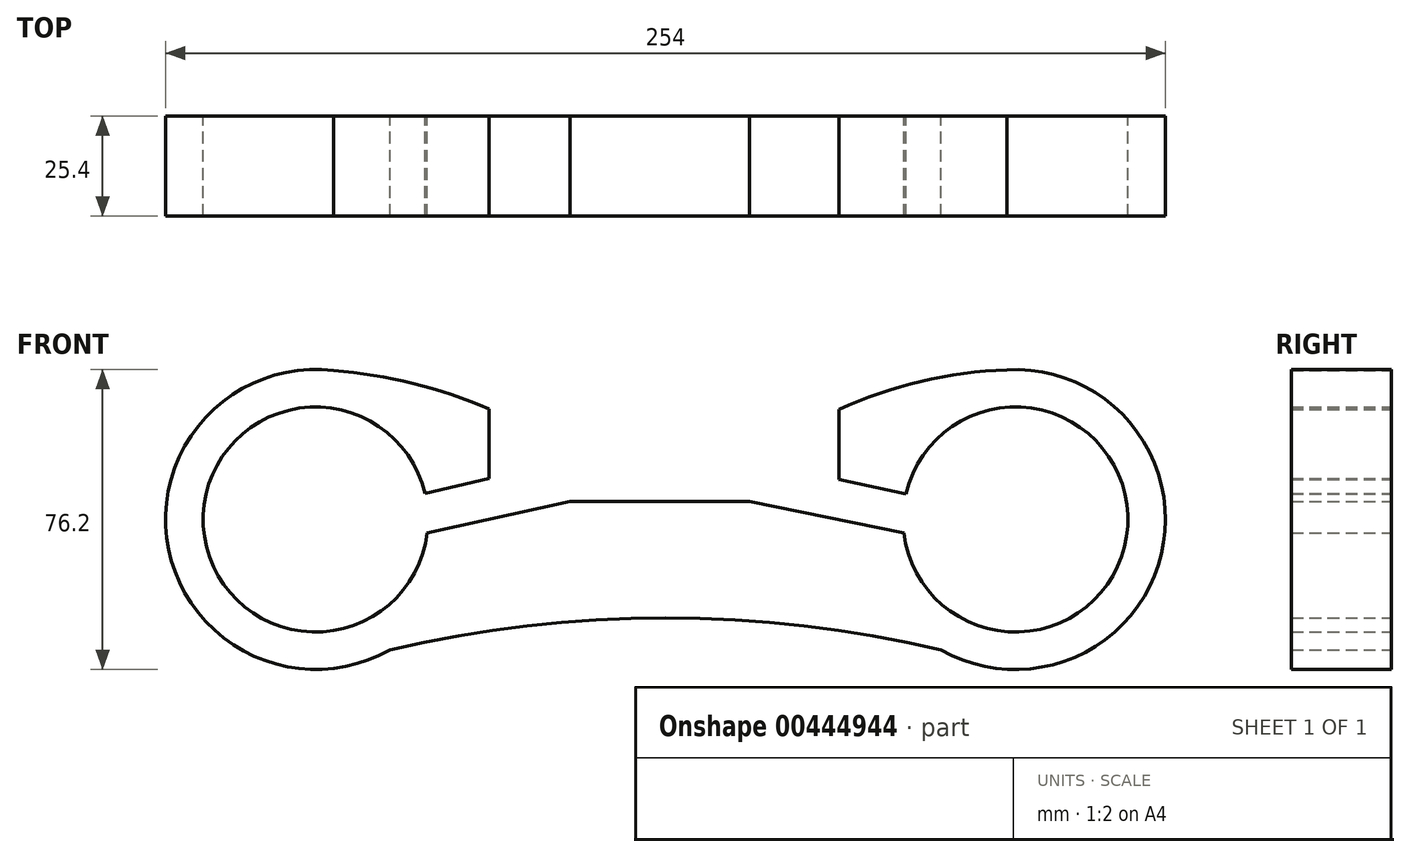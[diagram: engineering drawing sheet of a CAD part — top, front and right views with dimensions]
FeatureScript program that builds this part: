
annotation { "Feature Type Name" : "Feature", "Feature Type Description" : "" }
export const myFeature = defineFeature(function(context is Context, id is Id, definition is map)
    precondition{}
    {
        {
            var Q0;
            Q0=qCreatedBy(makeId("Front.planeOp"),FACE);
            var sketch = newSketch(context, id + "F0", { "sketchPlane" : qUnion([Q0])});
            skArc(sketch, "E0", {"start": v(-54.1, 9.54) * mm, "mid": v(-129.1, -2.98) * mm, "end": v(-53.1, -0.47) * mm});
            skArc(sketch, "E1", {"start": v(48.55, -0.64) * mm, "mid": v(124.55, -2.8) * mm, "end": v(49.5, 9.34) * mm});
            skArc(sketch, "E2", {"start": v(86.62, -37.3) * mm, "mid": v(-2.28, -24.27) * mm, "end": v(-91.18, -37.3) * mm});
            skArc(sketch, "E3", {"start": v(-63.38, 7.38) * mm, "mid": v(-119.7, -0.84) * mm, "end": v(-62.8, -2.6) * mm});
            skArc(sketch, "E4", {"start": v(58.25, -2.6) * mm, "mid": v(115.15, -0.8) * mm, "end": v(58.8, 7.33) * mm});
            skLineSegment(sketch, "E5", {"start": v(-26.59, 5.32) * mm, "end": v(19, 5.32) * mm});
            skLineSegment(sketch, "E6", {"start": v(-47.1, 11.17) * mm, "end": v(-63.38, 7.38) * mm});
            skLineSegment(sketch, "E7", {"start": v(-62.8, -2.6) * mm, "end": v(-26.59, 5.32) * mm});
            skLineSegment(sketch, "E8", {"start": v(41.8, 11) * mm, "end": v(58.8, 7.33) * mm});
            skLineSegment(sketch, "E9", {"start": v(58.25, -2.6) * mm, "end": v(19, 5.32) * mm});
            skLineSegment(sketch, "E10.top", {"start": v(-27.55, 5.11) * mm, "end": v(20.05, 5.11) * mm});
            skLineSegment(sketch, "E10.left", {"start": v(-47.1, 28.9) * mm, "end": v(-47.1, 11.17) * mm});
            skLineSegment(sketch, "E10.right", {"start": v(41.8, 28.8) * mm, "end": v(41.8, 11) * mm});
            skPoint(sketch, "E11.orphan", {"position": v(-26.59, 26.55) * mm});
            skPoint(sketch, "E12.orphan", {"position": v(-26.59, 15.94) * mm});
            skPoint(sketch, "E13.orphan", {"position": v(-72.23, 5.32) * mm});
            skPoint(sketch, "E14.orphan", {"position": v(-70.03, -4.17) * mm});
            skPoint(sketch, "E15.orphan", {"position": v(68.07, 5.32) * mm});
            skPoint(sketch, "E16.orphan", {"position": v(66.02, -4.17) * mm});
            skPoint(sketch, "E17.end.orphan", {"position": v(19, 15.94) * mm});
            skPoint(sketch, "E18.start.orphan", {"position": v(-91.18, 38.9) * mm});
            skPoint(sketch, "E19.trimOffspring.end.orphan", {"position": v(86.62, 38.9) * mm});
            skArc(sketch, "E20", {"start": v(-47.1, 28.9) * mm, "mid": v(-68.69, 35.9) * mm, "end": v(-91.18, 38.9) * mm});
            skArc(sketch, "E21", {"start": v(86.62, 38.9) * mm, "mid": v(63.7, 36.12) * mm, "end": v(41.8, 28.8) * mm});
            skSolve(sketch);
        }
        {
            var Q0;
            Q0 = qSketchRegion(id + "F0", true);
            extrude(context, id + "F1", {"entities" : qUnion([Q0]), "depth" : 25.4 * mm});
        }
    });
